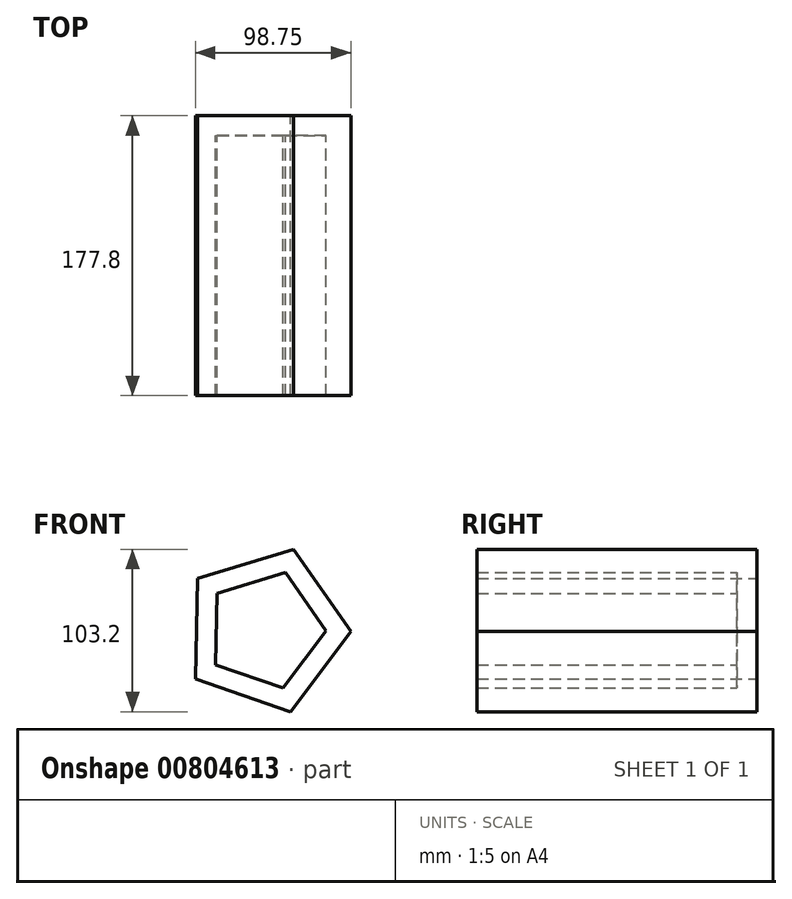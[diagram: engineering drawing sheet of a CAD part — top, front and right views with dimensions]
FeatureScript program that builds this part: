
annotation { "Feature Type Name" : "Feature", "Feature Type Description" : "" }
export const myFeature = defineFeature(function(context is Context, id is Id, definition is map)
    precondition{}
    {
        {
            var Q0;
            Q0=qCreatedBy(makeId("Front.planeOp"),FACE);
            var sketch = newSketch(context, id + "F0", { "sketchPlane" : qUnion([Q0])});
            skCircle(sketch, "E0.cCircle", {"center": v(-82.18, -11.8) * mm, "radius": 43.9 * mm, "construction": true});
            skLineSegment(sketch, "E0.0", {"start": v(-64.45, 39.49) * mm, "end": v(-27.92, -12.81) * mm});
            skLineSegment(sketch, "E0.1", {"start": v(-27.92, -12.81) * mm, "end": v(-66.38, -63.71) * mm});
            skLineSegment(sketch, "E0.2", {"start": v(-66.38, -63.71) * mm, "end": v(-126.67, -42.87) * mm});
            skLineSegment(sketch, "E0.3", {"start": v(-126.67, -42.87) * mm, "end": v(-125.48, 20.92) * mm});
            skLineSegment(sketch, "E0.4", {"start": v(-125.48, 20.92) * mm, "end": v(-64.45, 39.49) * mm});
            skPoint(sketch, "E0.0.midPoint", {"position": v(-46.19, 13.34) * mm});
            skSolve(sketch);
        }
        {
            var Q0;
            Q0=makeQuery(id+"F0.imprint","IMPRINT",FACE,{"disambiguationData":[TD([[makeQuery(id+"F0.imprint","IMPRINT",EDGE,{"derivedFrom":sQuery(id+"F0.wireOp",EDGE,"E0.0")}),-1.0]])]});
            extrude(context, id + "F1", {"entities" : qUnion([Q0]), "depth" : 177.8 * mm, "offsetDistance" : 25.4 * mm});
        }
        {
            var Q0;
            Q0=makeQuery(id+"F1.opExtrude","CAP_FACE",FACE,{"disambiguationData":[OSD([sQuery(id+"F0.wireOp",EDGE,"E0.0"),sQuery(id+"F0.wireOp",EDGE,"E0.1"),sQuery(id+"F0.wireOp",EDGE,"E0.2"),sQuery(id+"F0.wireOp",EDGE,"E0.3"),sQuery(id+"F0.wireOp",EDGE,"E0.4")])],"isStart":false});
            shell(context, id + "F2", {"entities" : qUnion([Q0]), "thickness" : 12.7 * mm});
        }
    });
